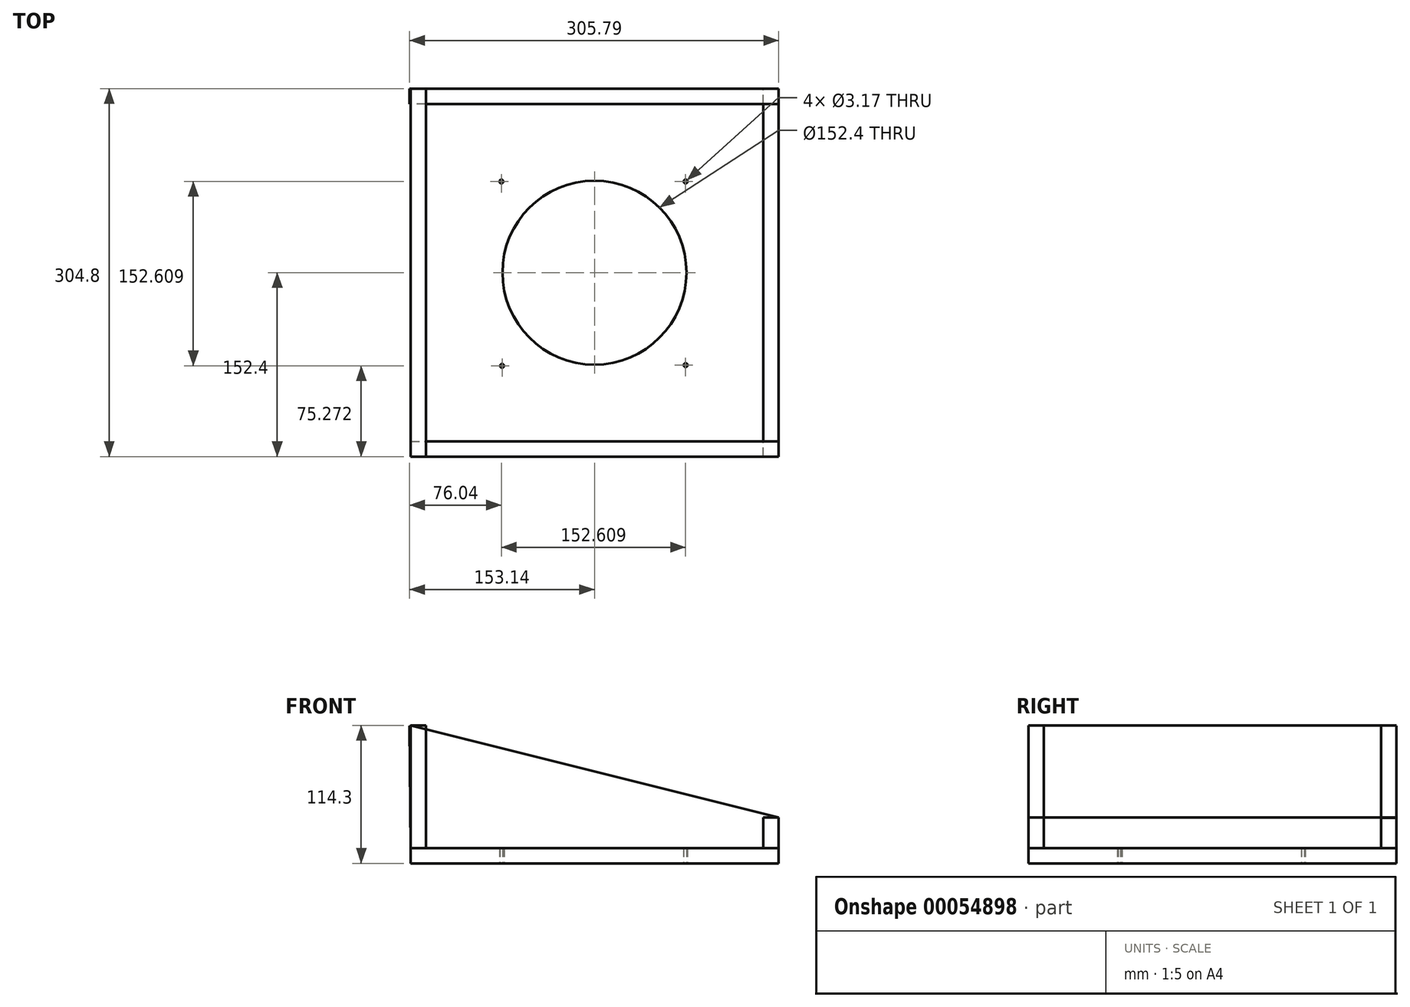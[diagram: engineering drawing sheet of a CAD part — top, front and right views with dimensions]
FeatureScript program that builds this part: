
annotation { "Feature Type Name" : "Feature", "Feature Type Description" : "" }
export const myFeature = defineFeature(function(context is Context, id is Id, definition is map)
    precondition{}
    {
        {
            var Q0;
            Q0=qCreatedBy(makeId("Top.planeOp"),FACE);
            var sketch = newSketch(context, id + "F0", { "sketchPlane" : qUnion([Q0])});
            skLineSegment(sketch, "E0.rect.bottom", {"start": v(152.4, -152.4) * mm, "end": v(-152.4, -152.4) * mm});
            skLineSegment(sketch, "E0.rect.top", {"start": v(152.4, 152.4) * mm, "end": v(-152.4, 152.4) * mm});
            skLineSegment(sketch, "E0.rect.left", {"start": v(152.4, -152.4) * mm, "end": v(152.4, 152.4) * mm});
            skLineSegment(sketch, "E0.rect.right", {"start": v(-152.4, -152.4) * mm, "end": v(-152.4, 152.4) * mm});
            skPoint(sketch, "E0.rect.middle", {"position": v(0, 0) * mm});
            skCircle(sketch, "E1", {"center": v(0, 0) * mm, "radius": 76.2 * mm});
            skSolve(sketch);
        }
        {
            var Q0;
            Q0=makeQuery(id+"F0.imprint","IMPRINT",FACE,{"disambiguationData":[TD([[makeQuery(id+"F0.imprint","IMPRINT",EDGE,{"derivedFrom":sQuery(id+"F0.wireOp",EDGE,"E0.rect.bottom")}),-1.0]])]});
            extrude(context, id + "F1", {"entities" : qUnion([Q0]), "depth" : 12.7 * mm});
        }
        {
            var Q0;
            Q0=makeQuery(id+"F1.opExtrude","SWEPT_FACE",FACE,{"disambiguationData":[OSD([sQuery(id+"F0.wireOp",EDGE,"E0.rect.bottom")])]});
            var sketch = newSketch(context, id + "F2", { "sketchPlane" : qUnion([Q0])});
            skLineSegment(sketch, "E2", {"start": v(-152.4, 12.7) * mm, "end": v(-152.4, 114.3) * mm});
            skLineSegment(sketch, "E3", {"start": v(-152.4, 114.3) * mm, "end": v(152.65, 38.1) * mm});
            skLineSegment(sketch, "E4", {"start": v(152.65, 38.1) * mm, "end": v(152.4, 12.7) * mm});
            skSolve(sketch);
        }
        {
            var Q0;
            Q0=makeQuery(id+"F1.opExtrude","SWEPT_FACE",FACE,{"disambiguationData":[OSD([sQuery(id+"F0.wireOp",EDGE,"E0.rect.right")])]});
            var sketch = newSketch(context, id + "F3", { "sketchPlane" : qUnion([Q0])});
            skLineSegment(sketch, "E5.bottom", {"start": v(152.4, 12.7) * mm, "end": v(-152.4, 12.7) * mm});
            skLineSegment(sketch, "E5.top", {"start": v(152.4, 114.3) * mm, "end": v(-152.4, 114.3) * mm});
            skLineSegment(sketch, "E5.left", {"start": v(152.4, 12.7) * mm, "end": v(152.4, 114.3) * mm});
            skLineSegment(sketch, "E5.right", {"start": v(-152.4, 12.7) * mm, "end": v(-152.4, 114.3) * mm});
            skSolve(sketch);
        }
        {
            var Q0;
            Q0=makeQuery(id+"F1.opExtrude","SWEPT_FACE",FACE,{"disambiguationData":[OSD([sQuery(id+"F0.wireOp",EDGE,"E0.rect.left")])]});
            var sketch = newSketch(context, id + "F4", { "sketchPlane" : qUnion([Q0])});
            skLineSegment(sketch, "E6.bottom", {"start": v(-152.4, 12.7) * mm, "end": v(152.4, 12.7) * mm});
            skLineSegment(sketch, "E6.top", {"start": v(-152.4, 38.1) * mm, "end": v(152.4, 38.1) * mm});
            skLineSegment(sketch, "E6.left", {"start": v(-152.4, 12.7) * mm, "end": v(-152.4, 38.1) * mm});
            skLineSegment(sketch, "E6.right", {"start": v(152.4, 12.7) * mm, "end": v(152.4, 38.1) * mm});
            skSolve(sketch);
        }
        {
            var Q0;
            Q0=makeQuery(id+"F1.opExtrude","SWEPT_FACE",FACE,{"disambiguationData":[OSD([sQuery(id+"F0.wireOp",EDGE,"E0.rect.top")])]});
            var sketch = newSketch(context, id + "F5", { "sketchPlane" : qUnion([Q0])});
            skLineSegment(sketch, "E7", {"start": v(-152.4, 12.7) * mm, "end": v(-152.4, 37.52) * mm});
            skLineSegment(sketch, "E8", {"start": v(-152.4, 37.52) * mm, "end": v(153.14, 113.81) * mm});
            skLineSegment(sketch, "E9", {"start": v(153.14, 113.81) * mm, "end": v(152.4, 12.7) * mm});
            skSolve(sketch);
        }
        {
            var Q0;
            Q0=makeQuery(id+"F2.imprint","IMPRINT",FACE,{"disambiguationData":[TD([[makeQuery(id+"F2.imprint","IMPRINT",EDGE,{"derivedFrom":sQuery(id+"F2.wireOp",EDGE,"E2")}),-1.0]])]});
            extrude(context, id + "F6", {"entities" : qUnion([Q0]), "oppositeDirection" : true, "depth" : 12.7 * mm});
        }
        {
            var Q0;
            Q0=makeQuery(id+"F5.imprint","IMPRINT",FACE,{"disambiguationData":[TD([[makeQuery(id+"F5.imprint","IMPRINT",EDGE,{"derivedFrom":sQuery(id+"F5.wireOp",EDGE,"E7")}),-1.0]])]});
            extrude(context, id + "F7", {"entities" : qUnion([Q0]), "oppositeDirection" : true, "depth" : 12.7 * mm});
        }
        {
            var Q0;
            Q0=makeQuery(id+"F3.imprint","IMPRINT",FACE,{"disambiguationData":[TD([[makeQuery(id+"F3.imprint","IMPRINT",EDGE,{"derivedFrom":sQuery(id+"F3.wireOp",EDGE,"E5.bottom")}),-1.0]])]});
            var sketch = newSketch(context, id + "F8", { "sketchPlane" : qUnion([Q0])});
            skSolve(sketch);
        }
        {
            var Q0;
            Q0=makeQuery(id+"F4.imprint","IMPRINT",FACE,{"disambiguationData":[TD([[makeQuery(id+"F4.imprint","IMPRINT",EDGE,{"derivedFrom":sQuery(id+"F4.wireOp",EDGE,"E6.bottom")}),1.0]])]});
            extrude(context, id + "F9", {"entities" : qUnion([Q0]), "oppositeDirection" : true, "depth" : 12.7 * mm});
        }
        {
            var Q0;
            Q0=makeQuery(id+"F8.imprint","IMPRINT",FACE,{"disambiguationData":[TD([[makeQuery(id+"F8.imprint","IMPRINT",EDGE,{"derivedFrom":makeQuery(id+"F3.imprint","IMPRINT",EDGE,{"derivedFrom":sQuery(id+"F3.wireOp",EDGE,"E5.bottom")})}),-1.0]])]});
            extrude(context, id + "F10", {"entities" : qUnion([Q0]), "oppositeDirection" : true, "depth" : 12.7 * mm});
        }
        {
            var Q0;
            Q0=makeQuery(id+"F1.opExtrude","CAP_FACE",FACE,{"disambiguationData":[OSD([sQuery(id+"F0.wireOp",EDGE,"E0.rect.bottom"),sQuery(id+"F0.wireOp",EDGE,"E0.rect.top"),sQuery(id+"F0.wireOp",EDGE,"E0.rect.left"),sQuery(id+"F0.wireOp",EDGE,"E0.rect.right"),sQuery(id+"F0.wireOp",EDGE,"E1")])],"isStart":true});
            var sketch = newSketch(context, id + "F11", { "sketchPlane" : qUnion([Q0])});
            skPoint(sketch, "E10", {"position": v(-76.55, 77.13) * mm});
            skPoint(sketch, "E11", {"position": v(75.5, 76.58) * mm});
            skPoint(sketch, "E12", {"position": v(75.5, -75.48) * mm});
            skPoint(sketch, "E13", {"position": v(-77.1, -75.48) * mm});
            skSolve(sketch);
        }
        {
            var Q0;
            Q0=sQuery(id+"F11.wireOp",VERTEX,"E10");
            var Q1;
            Q1=sQuery(id+"F11.wireOp",VERTEX,"E11");
            var Q2;
            Q2=sQuery(id+"F11.wireOp",VERTEX,"E12");
            var Q3;
            Q3=sQuery(id+"F11.wireOp",VERTEX,"E13");
            var Q4;
            Q4=makeQuery(id+"F1.opExtrude","SWEPT_BODY",BODY,{"disambiguationData":[OSD([sQuery(id+"F0.wireOp",EDGE,"E0.rect.bottom"),sQuery(id+"F0.wireOp",EDGE,"E0.rect.top"),sQuery(id+"F0.wireOp",EDGE,"E0.rect.left"),sQuery(id+"F0.wireOp",EDGE,"E0.rect.right"),sQuery(id+"F0.wireOp",EDGE,"E1")])]});
            hole(context, id + "F12", {"style" : HoleStyle.SIMPLE, "holeDiameter" : 3.17 * mm, "endStyle" : HoleEndStyle.THROUGH, "locations" : qUnion([Q0, Q1, Q2, Q3]), "scope" : qUnion([Q4])});
        }
    });
